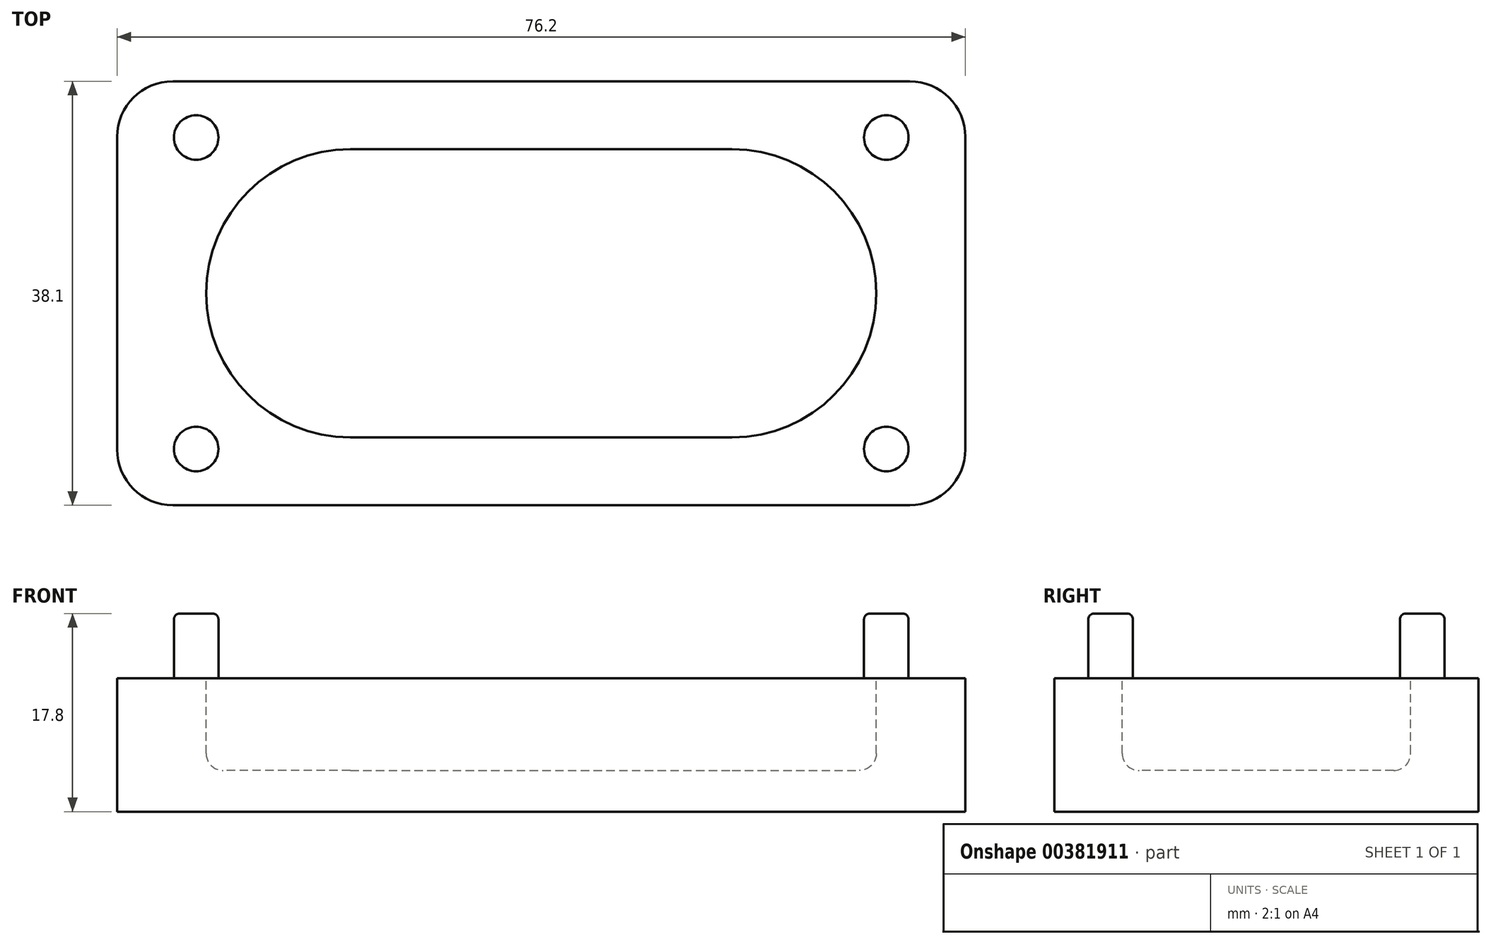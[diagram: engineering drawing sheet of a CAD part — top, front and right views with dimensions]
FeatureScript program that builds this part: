
annotation { "Feature Type Name" : "Feature", "Feature Type Description" : "" }
export const myFeature = defineFeature(function(context is Context, id is Id, definition is map)
    precondition{}
    {
        {
            var Q0;
            Q0=qCreatedBy(makeId("Top.planeOp"),FACE);
            var sketch = newSketch(context, id + "F0", { "sketchPlane" : qUnion([Q0])});
            skLineSegment(sketch, "E0.bottom", {"start": v(-33.1, 19.05) * mm, "end": v(33.1, 19.05) * mm});
            skLineSegment(sketch, "E0.top", {"start": v(-33.1, -19.05) * mm, "end": v(33.1, -19.05) * mm});
            skLineSegment(sketch, "E0.left", {"start": v(-38.1, 14.05) * mm, "end": v(-38.1, -14.05) * mm});
            skLineSegment(sketch, "E0.right", {"start": v(38.1, 14.05) * mm, "end": v(38.1, -14.05) * mm});
            skPoint(sketch, "E0.middle", {"position": v(0, 0) * mm});
            skPoint(sketch, "E1.visualSharp", {"position": v(-38.1, 19.05) * mm});
            skArc(sketch, "E1.filletArc", {"start": v(-33.1, 19.05) * mm, "mid": v(-36.64, 17.59) * mm, "end": v(-38.1, 14.05) * mm});
            skPoint(sketch, "E2.visualSharp", {"position": v(-38.1, -19.05) * mm});
            skArc(sketch, "E2.filletArc", {"start": v(-38.1, -14.05) * mm, "mid": v(-36.64, -17.59) * mm, "end": v(-33.1, -19.05) * mm});
            skPoint(sketch, "E3.visualSharp", {"position": v(38.1, -19.05) * mm});
            skArc(sketch, "E3.filletArc", {"start": v(33.1, -19.05) * mm, "mid": v(36.64, -17.59) * mm, "end": v(38.1, -14.05) * mm});
            skPoint(sketch, "E4.visualSharp", {"position": v(38.1, 19.05) * mm});
            skArc(sketch, "E4.filletArc", {"start": v(38.1, 14.05) * mm, "mid": v(36.64, 17.59) * mm, "end": v(33.1, 19.05) * mm});
            skSolve(sketch);
        }
        {
            var Q0;
            Q0=makeQuery(id+"F0.imprint","IMPRINT",FACE,{"disambiguationData":[TD([[makeQuery(id+"F0.imprint","IMPRINT",EDGE,{"derivedFrom":sQuery(id+"F0.wireOp",EDGE,"E0.bottom")}),-1.0]])]});
            extrude(context, id + "F1", {"entities" : qUnion([Q0]), "depth" : -12 * mm});
        }
        {
            var Q0;
            Q0=qCreatedBy(makeId("Top.planeOp"),FACE);
            var sketch = newSketch(context, id + "F2", { "sketchPlane" : qUnion([Q0])});
            skLineSegment(sketch, "E5.bottom", {"start": v(-17.15, 12.95) * mm, "end": v(17.14, 12.95) * mm});
            skLineSegment(sketch, "E5.top", {"start": v(-17.15, -12.95) * mm, "end": v(17.14, -12.95) * mm});
            skLineSegment(sketch, "E5.left", {"start": v(-30.1, 0) * mm, "end": v(-30.1, 0) * mm});
            skLineSegment(sketch, "E5.right", {"start": v(30.1, 0) * mm, "end": v(30.1, 0) * mm});
            skPoint(sketch, "E5.middle", {"position": v(0, 0) * mm});
            skPoint(sketch, "E6.visualSharp", {"position": v(-30.1, 12.95) * mm});
            skArc(sketch, "E6.filletArc", {"start": v(-17.15, 12.95) * mm, "mid": v(-26.3, 9.16) * mm, "end": v(-30.1, 0) * mm});
            skPoint(sketch, "E7.visualSharp", {"position": v(-30.1, -12.95) * mm});
            skArc(sketch, "E7.filletArc", {"start": v(-30.1, 0) * mm, "mid": v(-26.3, -9.16) * mm, "end": v(-17.15, -12.95) * mm});
            skPoint(sketch, "E8.visualSharp", {"position": v(30.1, -12.95) * mm});
            skArc(sketch, "E8.filletArc", {"start": v(17.14, -12.95) * mm, "mid": v(26.3, -9.16) * mm, "end": v(30.1, 0) * mm});
            skPoint(sketch, "E9.visualSharp", {"position": v(30.1, 12.95) * mm});
            skArc(sketch, "E9.filletArc", {"start": v(30.1, 0) * mm, "mid": v(26.3, 9.16) * mm, "end": v(17.14, 12.95) * mm});
            skSolve(sketch);
        }
        {
            var Q0;
            Q0=makeQuery(id+"F2.imprint","IMPRINT",FACE,{"disambiguationData":[TD([[makeQuery(id+"F2.imprint","IMPRINT",EDGE,{"derivedFrom":sQuery(id+"F2.wireOp",EDGE,"E5.bottom")}),-1.0]])]});
            extrude(context, id + "F3", {"entities" : qUnion([Q0]), "operationType" : NewBodyOperationType.REMOVE, "oppositeDirection" : true, "depth" : 8.3 * mm});
        }
        {
            var Q0;
            Q0=makeQuery(id+"F3.boolean.opBoolean","COPY",EDGE,{"derivedFrom":makeQuery(id+"F3.opExtrude","CAP_EDGE",EDGE,{"disambiguationData":[OSD([sQuery(id+"F2.wireOp",EDGE,"E5.bottom")])],"isStart":false})});
            var Q1;
            Q1=makeQuery(id+"F3.boolean.opBoolean","COPY",EDGE,{"derivedFrom":makeQuery(id+"F3.opExtrude","CAP_EDGE",EDGE,{"disambiguationData":[OSD([sQuery(id+"F2.wireOp",EDGE,"E6.filletArc")])],"isStart":false})});
            var Q2;
            Q2=makeQuery(id+"F3.boolean.opBoolean","COPY",EDGE,{"derivedFrom":makeQuery(id+"F3.opExtrude","CAP_EDGE",EDGE,{"disambiguationData":[OSD([sQuery(id+"F2.wireOp",EDGE,"E5.left")])],"isStart":false})});
            var Q3;
            Q3=makeQuery(id+"F3.boolean.opBoolean","COPY",EDGE,{"derivedFrom":makeQuery(id+"F3.opExtrude","CAP_EDGE",EDGE,{"disambiguationData":[OSD([sQuery(id+"F2.wireOp",EDGE,"E7.filletArc")])],"isStart":false})});
            var Q4;
            Q4=makeQuery(id+"F3.boolean.opBoolean","COPY",EDGE,{"derivedFrom":makeQuery(id+"F3.opExtrude","CAP_EDGE",EDGE,{"disambiguationData":[OSD([sQuery(id+"F2.wireOp",EDGE,"E5.top")])],"isStart":false})});
            var Q5;
            Q5=makeQuery(id+"F3.boolean.opBoolean","COPY",EDGE,{"derivedFrom":makeQuery(id+"F3.opExtrude","CAP_EDGE",EDGE,{"disambiguationData":[OSD([sQuery(id+"F2.wireOp",EDGE,"E9.filletArc")])],"isStart":false})});
            var Q6;
            Q6=makeQuery(id+"F3.boolean.opBoolean","COPY",EDGE,{"derivedFrom":makeQuery(id+"F3.opExtrude","CAP_EDGE",EDGE,{"disambiguationData":[OSD([sQuery(id+"F2.wireOp",EDGE,"E5.right")])],"isStart":false})});
            var Q7;
            Q7=makeQuery(id+"F3.boolean.opBoolean","COPY",EDGE,{"derivedFrom":makeQuery(id+"F3.opExtrude","CAP_EDGE",EDGE,{"disambiguationData":[OSD([sQuery(id+"F2.wireOp",EDGE,"E8.filletArc")])],"isStart":false})});
            fillet(context, id + "F4", {"entities" : qUnion([Q0, Q1, Q2, Q3, Q4, Q5, Q6, Q7]), "radius" : 1.52 * mm, "tangentPropagation" : true, "allowEdgeOverflow" : false});
        }
        {
            var Q0;
            Q0=qCreatedBy(makeId("Top.planeOp"),FACE);
            var sketch = newSketch(context, id + "F5", { "sketchPlane" : qUnion([Q0])});
            skCircle(sketch, "E10", {"center": v(-31, 14) * mm, "radius": 2 * mm});
            skCircle(sketch, "E11", {"center": v(-31, -14) * mm, "radius": 2 * mm});
            skCircle(sketch, "E12", {"center": v(31, 14) * mm, "radius": 2 * mm});
            skCircle(sketch, "E13", {"center": v(31, -14) * mm, "radius": 2 * mm});
            skPoint(sketch, "E14.middle", {"position": v(0, 0) * mm});
            skLineSegment(sketch, "E15.bottom", {"start": v(-31, 14) * mm, "end": v(31, 14) * mm});
            skLineSegment(sketch, "E15.top", {"start": v(-31, -14) * mm, "end": v(31, -14) * mm});
            skLineSegment(sketch, "E15.left", {"start": v(-31, 14) * mm, "end": v(-31, -14) * mm});
            skLineSegment(sketch, "E15.right", {"start": v(31, 14) * mm, "end": v(31, -14) * mm});
            skSolve(sketch);
        }
        {
            var Q0;
            Q0=makeQuery(id+"F5.imprint","IMPRINT",FACE,{"disambiguationData":[TD([[makeQuery(id+"F5.imprint","IMPRINT",EDGE,{"derivedFrom":sQuery(id+"F5.wireOp",EDGE,"E10")}),1.0]])]});
            var Q1;
            Q1=makeQuery(id+"F5.imprint","IMPRINT",FACE,{"disambiguationData":[TD([[makeQuery(id+"F5.imprint","IMPRINT",EDGE,{"derivedFrom":sQuery(id+"F5.wireOp",EDGE,"E12")}),1.0]])]});
            var Q2;
            Q2=makeQuery(id+"F5.imprint","IMPRINT",FACE,{"disambiguationData":[TD([[makeQuery(id+"F5.imprint","IMPRINT",EDGE,{"derivedFrom":sQuery(id+"F5.wireOp",EDGE,"E13")}),1.0]])]});
            var Q3;
            Q3=makeQuery(id+"F5.imprint","IMPRINT",FACE,{"disambiguationData":[TD([[makeQuery(id+"F5.imprint","IMPRINT",EDGE,{"derivedFrom":sQuery(id+"F5.wireOp",EDGE,"E11")}),1.0]])]});
            var Q4;
            Q4=sQuery(id+"F5.wireOp",EDGE,"E10");
            var Q5;
            Q5=sQuery(id+"F5.wireOp",EDGE,"E11");
            var Q6;
            Q6=sQuery(id+"F5.wireOp",EDGE,"E12");
            var Q7;
            Q7=sQuery(id+"F5.wireOp",EDGE,"E13");
            extrude(context, id + "F6", {"entities" : qUnion([Q0, Q1, Q2, Q3]), "operationType" : NewBodyOperationType.ADD, "surfaceEntities" : qUnion([Q4, Q5, Q6, Q7]), "depth" : 5.8 * mm});
        }
        {
            var Q0;
            Q0=makeQuery(id+"F6.opExtrude","CAP_FACE",FACE,{"disambiguationData":[OSD([sQuery(id+"F5.wireOp",EDGE,"E10")])],"isStart":false});
            var Q1;
            Q1=makeQuery(id+"F6.opExtrude","CAP_FACE",FACE,{"disambiguationData":[OSD([sQuery(id+"F5.wireOp",EDGE,"E11")])],"isStart":false});
            var Q2;
            Q2=makeQuery(id+"F6.opExtrude","CAP_FACE",FACE,{"disambiguationData":[OSD([sQuery(id+"F5.wireOp",EDGE,"E13")])],"isStart":false});
            var Q3;
            Q3=makeQuery(id+"F6.opExtrude","CAP_FACE",FACE,{"disambiguationData":[OSD([sQuery(id+"F5.wireOp",EDGE,"E12")])],"isStart":false});
            fillet(context, id + "F7", {"entities" : qUnion([Q0, Q1, Q2, Q3]), "radius" : 0.5 * mm, "tangentPropagation" : true, "allowEdgeOverflow" : false});
        }
    });
